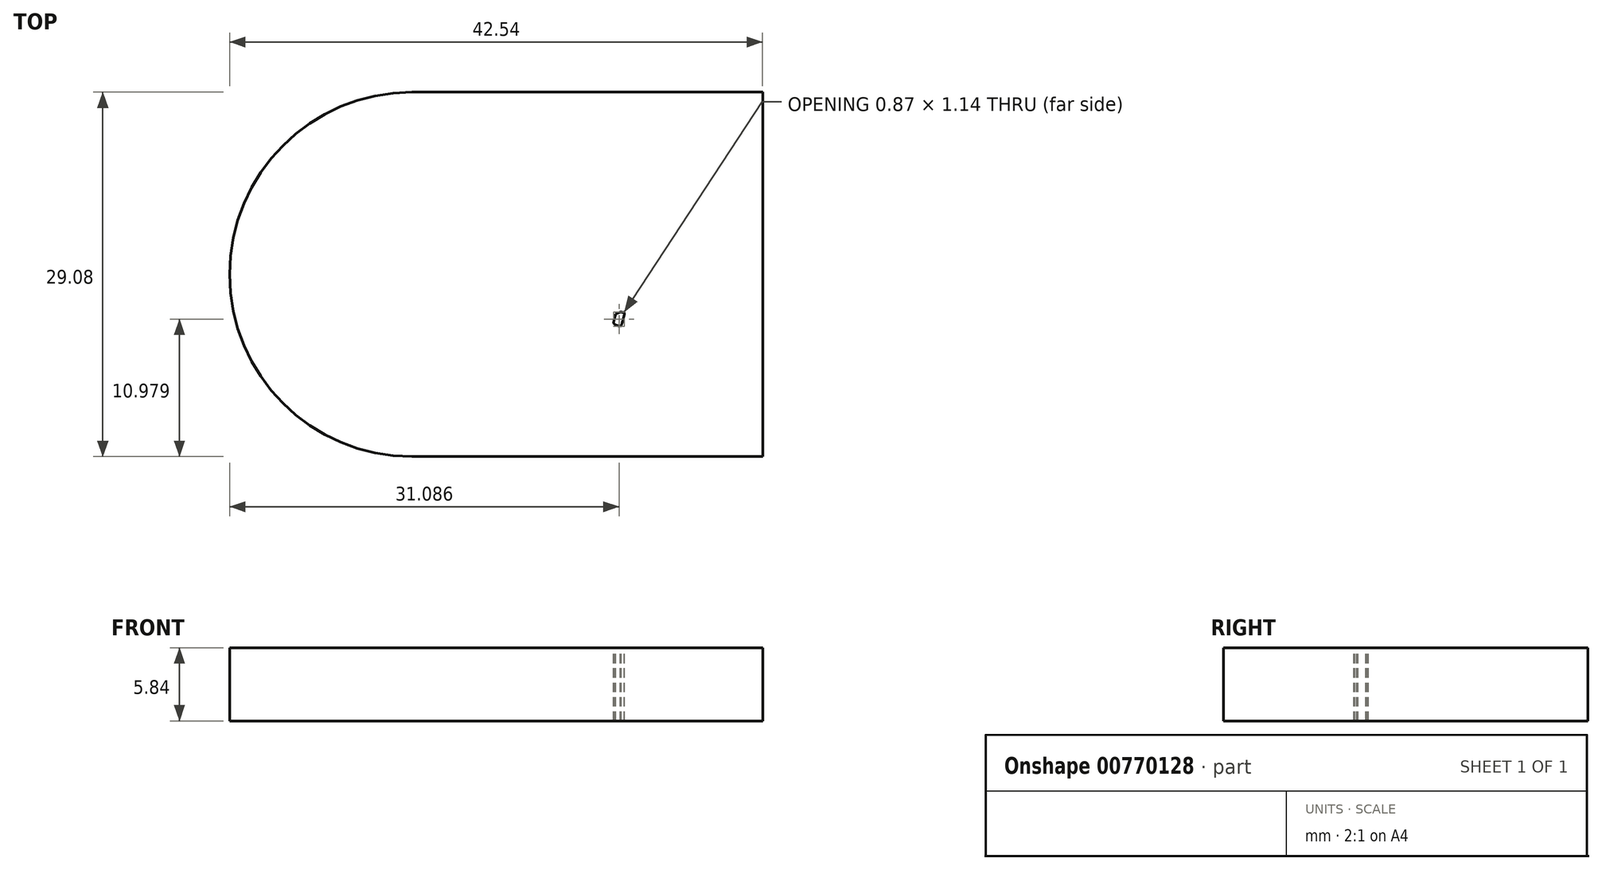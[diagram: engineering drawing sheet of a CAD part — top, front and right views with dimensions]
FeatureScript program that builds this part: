
annotation { "Feature Type Name" : "Feature", "Feature Type Description" : "" }
export const myFeature = defineFeature(function(context is Context, id is Id, definition is map)
    precondition{}
    {
        {
            var Q0;
            Q0=qCreatedBy(makeId("Top.planeOp"),FACE);
            var sketch = newSketch(context, id + "F0", { "sketchPlane" : qUnion([Q0])});
            skLineSegment(sketch, "E0", {"start": v(-14.54, 0) * mm, "end": v(28, 0) * mm, "construction": true});
            skLineSegment(sketch, "E1", {"start": v(0, -14.54) * mm, "end": v(28, -14.54) * mm});
            skLineSegment(sketch, "E2", {"start": v(0, 14.54) * mm, "end": v(28, 14.54) * mm});
            skLineSegment(sketch, "E3", {"start": v(28, -14.54) * mm, "end": v(28, 14.54) * mm});
            skArc(sketch, "E4", {"start": v(0, 14.54) * mm, "mid": v(-14.54, 0) * mm, "end": v(0, -14.54) * mm});
            skSolve(sketch);
        }
        {
            var Q0;
            Q0=makeQuery(id+"F0.imprint","IMPRINT",FACE,{"disambiguationData":[TD([[makeQuery(id+"F0.imprint","IMPRINT",EDGE,{"derivedFrom":sQuery(id+"F0.wireOp",EDGE,"E1")}),1.0]])]});
            extrude(context, id + "F1", {"entities" : qUnion([Q0]), "oppositeDirection" : true, "depth" : 5.84 * mm, "offsetDistance" : 25.4 * mm});
        }
        {
            var Q0;
            Q0=makeQuery(id+"F1.opExtrude","CAP_FACE",FACE,{"disambiguationData":[OSD([sQuery(id+"F0.wireOp",EDGE,"E1"),sQuery(id+"F0.wireOp",EDGE,"E2"),sQuery(id+"F0.wireOp",EDGE,"E3"),sQuery(id+"F0.wireOp",EDGE,"E4")])],"isStart":true});
            var sketch = newSketch(context, id + "F2", { "sketchPlane" : qUnion([Q0])});
            skFitSpline(sketch, "E5", {"points": [v(-3.35, 10.84) * mm, v(-3.23, 11.27) * mm, v(-2.96, 11.36) * mm, v(-2.58, 11.1) * mm]});
            skFitSpline(sketch, "E6", {"points": [v(-2.58, 11.1) * mm, v(-2.42, 11) * mm, v(-2.3, 10.84) * mm, v(-2.1, 10.48) * mm]});
            skFitSpline(sketch, "E7", {"points": [v(-2.1, 10.48) * mm, v(-1.72, 9.81) * mm, v(-1.53, 9.62) * mm, v(-0.8, 9.13) * mm]});
            skFitSpline(sketch, "E8", {"points": [v(-0.8, 9.13) * mm, v(-0.1, 8.66) * mm, v(0.98, 7.86) * mm, v(1.93, 7.1) * mm]});
            skFitSpline(sketch, "E9", {"points": [v(2.93, 6.55) * mm, v(3.7, 6.5) * mm, v(4.42, 6.3) * mm, v(4.64, 6.06) * mm]});
            skFitSpline(sketch, "E10", {"points": [v(4.64, 6.06) * mm, v(4.71, 5.99) * mm, v(5.07, 5.55) * mm, v(5.43, 5.1) * mm]});
            skFitSpline(sketch, "E11", {"points": [v(5.43, 5.1) * mm, v(5.95, 4.45) * mm, v(6.1, 4.23) * mm, v(6.16, 4.02) * mm]});
            skFitSpline(sketch, "E12", {"points": [v(6.16, 4.02) * mm, v(6.2, 3.87) * mm, v(6.34, 3.63) * mm, v(6.48, 3.45) * mm]});
            skFitSpline(sketch, "E13", {"points": [v(6.48, 3.45) * mm, v(6.6, 3.28) * mm, v(6.84, 2.92) * mm, v(7, 2.64) * mm]});
            skFitSpline(sketch, "E14", {"points": [v(7, 2.64) * mm, v(7.2, 2.28) * mm, v(7.3, 2.13) * mm, v(7.42, 2.07) * mm]});
            skFitSpline(sketch, "E15", {"points": [v(7.42, 2.07) * mm, v(7.52, 2.02) * mm, v(7.57, 1.96) * mm, v(7.58, 1.86) * mm]});
            skFitSpline(sketch, "E16", {"points": [v(7.58, 1.86) * mm, v(7.59, 1.75) * mm, v(7.7, 1.6) * mm, v(7.99, 1.31) * mm]});
            skLineSegment(sketch, "E17", {"start": v(1.93, 7.1) * mm, "end": v(2.59, 6.57) * mm});
            skLineSegment(sketch, "E18", {"start": v(2.59, 6.57) * mm, "end": v(2.93, 6.55) * mm});
            skFitSpline(sketch, "E19", {"points": [v(8.64, 0.91) * mm, v(8.87, 0.91) * mm, v(8.92, 0.93) * mm, v(9.07, 1.08) * mm]});
            skFitSpline(sketch, "E20", {"points": [v(9.07, 1.08) * mm, v(9.25, 1.27) * mm, v(9.28, 1.28) * mm, v(9.79, 1.35) * mm]});
            skFitSpline(sketch, "E21", {"points": [v(9.79, 1.35) * mm, v(10.73, 1.49) * mm, v(11, 1.5) * mm, v(12.04, 1.47) * mm]});
            skFitSpline(sketch, "E22", {"points": [v(12.04, 1.47) * mm, v(13.3, 1.44) * mm, v(13.45, 1.46) * mm, v(13.67, 1.72) * mm]});
            skFitSpline(sketch, "E23", {"points": [v(13.67, 1.72) * mm, v(13.84, 1.92) * mm, v(14.3, 2.78) * mm, v(14.68, 3.63) * mm]});
            skFitSpline(sketch, "E24", {"points": [v(14.68, 3.63) * mm, v(14.8, 3.9) * mm, v(14.97, 4.2) * mm, v(15.03, 4.27) * mm]});
            skFitSpline(sketch, "E25", {"points": [v(15.03, 4.27) * mm, v(15.15, 4.4) * mm, v(15.53, 4.55) * mm, v(15.74, 4.55) * mm]});
            skFitSpline(sketch, "E26", {"points": [v(15.74, 4.55) * mm, v(15.8, 4.55) * mm, v(15.92, 4.59) * mm, v(16.02, 4.64) * mm]});
            skFitSpline(sketch, "E27", {"points": [v(16.02, 4.64) * mm, v(16.24, 4.76) * mm, v(16.47, 4.76) * mm, v(16.83, 4.67) * mm]});
            skFitSpline(sketch, "E28", {"points": [v(16.83, 4.67) * mm, v(16.98, 4.63) * mm, v(17.22, 4.6) * mm, v(17.37, 4.6) * mm]});
            skFitSpline(sketch, "E29", {"points": [v(17.37, 4.6) * mm, v(17.82, 4.6) * mm, v(18.4, 4.41) * mm, v(19.13, 4.06) * mm]});
            skFitSpline(sketch, "E30", {"points": [v(19.13, 4.06) * mm, v(19.74, 3.76) * mm, v(20.28, 3.57) * mm, v(20.36, 3.65) * mm]});
            skFitSpline(sketch, "E31", {"points": [v(20.36, 3.65) * mm, v(20.38, 3.67) * mm, v(20.55, 5.16) * mm, v(20.56, 5.4) * mm]});
            skFitSpline(sketch, "E32", {"points": [v(20.56, 5.4) * mm, v(20.56, 5.5) * mm, v(20.94, 5.48) * mm, v(20.98, 5.39) * mm]});
            skFitSpline(sketch, "E33", {"points": [v(20.98, 5.39) * mm, v(21, 5.34) * mm, v(20.97, 4.92) * mm, v(20.93, 4.45) * mm]});
            skLineSegment(sketch, "E34", {"start": v(7.99, 1.31) * mm, "end": v(8.38, 0.91) * mm});
            skLineSegment(sketch, "E35", {"start": v(8.38, 0.91) * mm, "end": v(8.64, 0.91) * mm});
            skFitSpline(sketch, "E36", {"points": [v(21.04, 3.4) * mm, v(21.22, 3.22) * mm, v(21.24, 3.18) * mm, v(21.24, 2.97) * mm]});
            skFitSpline(sketch, "E37", {"points": [v(21.24, 2.97) * mm, v(21.24, 2.84) * mm, v(21.2, 2.6) * mm, v(21.14, 2.45) * mm]});
            skFitSpline(sketch, "E38", {"points": [v(21.14, 2.45) * mm, v(21.05, 2.16) * mm, v(21.05, 2.08) * mm, v(21.16, 2.08) * mm]});
            skFitSpline(sketch, "E39", {"points": [v(21.16, 2.08) * mm, v(21.2, 2.08) * mm, v(21.26, 2.04) * mm, v(21.3, 1.98) * mm]});
            skFitSpline(sketch, "E40", {"points": [v(21.3, 1.98) * mm, v(21.42, 1.86) * mm, v(21.34, 1.82) * mm, v(20.95, 1.79) * mm]});
            skLineSegment(sketch, "E41", {"start": v(20.93, 4.45) * mm, "end": v(20.84, 3.6) * mm});
            skLineSegment(sketch, "E42", {"start": v(20.84, 3.6) * mm, "end": v(21.04, 3.4) * mm});
            skFitSpline(sketch, "E43", {"points": [v(20.6, 1.52) * mm, v(20.58, 1.39) * mm, v(20.43, 0.22) * mm, v(20.27, -1.07) * mm]});
            skFitSpline(sketch, "E44", {"points": [v(20.27, -1.07) * mm, v(19.8, -4.88) * mm, v(19.4, -7.68) * mm, v(19.23, -8.27) * mm]});
            skFitSpline(sketch, "E45", {"points": [v(19.23, -8.27) * mm, v(19.18, -8.45) * mm, v(19.11, -8.56) * mm, v(19, -8.64) * mm]});
            skFitSpline(sketch, "E46", {"points": [v(19, -8.64) * mm, v(18.76, -8.81) * mm, v(18.73, -8.83) * mm, v(18.75, -8.73) * mm]});
            skFitSpline(sketch, "E47", {"points": [v(18.75, -8.73) * mm, v(18.86, -8.26) * mm, v(19.5, -3.67) * mm, v(19.88, -0.54) * mm]});
            skFitSpline(sketch, "E48", {"points": [v(19.88, -0.54) * mm, v(20.02, 0.54) * mm, v(20.14, 1.5) * mm, v(20.15, 1.6) * mm]});
            skFitSpline(sketch, "E49", {"points": [v(20.15, 1.6) * mm, v(20.18, 1.78) * mm, v(20.18, 1.78) * mm, v(20, 1.81) * mm]});
            skFitSpline(sketch, "E50", {"points": [v(20, 1.81) * mm, v(19.72, 1.86) * mm, v(19.5, 1.93) * mm, v(19.5, 1.98) * mm]});
            skFitSpline(sketch, "E51", {"points": [v(19.5, 1.98) * mm, v(19.5, 2.04) * mm, v(19.82, 2.12) * mm, v(20.04, 2.12) * mm]});
            skFitSpline(sketch, "E52", {"points": [v(20.04, 2.12) * mm, v(20.26, 2.12) * mm, v(20.27, 2.18) * mm, v(20.08, 2.4) * mm]});
            skFitSpline(sketch, "E53", {"points": [v(20.08, 2.4) * mm, v(20, 2.49) * mm, v(19.9, 2.65) * mm, v(19.88, 2.75) * mm]});
            skFitSpline(sketch, "E54", {"points": [v(19.88, 2.75) * mm, v(19.81, 2.98) * mm, v(19.82, 2.97) * mm, v(18.94, 3.14) * mm]});
            skFitSpline(sketch, "E55", {"points": [v(18.94, 3.14) * mm, v(18.22, 3.27) * mm, v(17.77, 3.3) * mm, v(17.39, 3.26) * mm]});
            skLineSegment(sketch, "E56", {"start": v(20.95, 1.79) * mm, "end": v(20.63, 1.76) * mm});
            skLineSegment(sketch, "E57", {"start": v(20.63, 1.76) * mm, "end": v(20.6, 1.52) * mm});
            skFitSpline(sketch, "E58", {"points": [v(17.1, 3) * mm, v(17.13, 2.75) * mm, v(17.1, 2.7) * mm, v(16.74, 2.5) * mm]});
            skFitSpline(sketch, "E59", {"points": [v(16.74, 2.5) * mm, v(16.48, 2.36) * mm, v(16.38, 2.08) * mm, v(16.35, 1.4) * mm]});
            skFitSpline(sketch, "E60", {"points": [v(16.35, 1.4) * mm, v(16.32, 0.8) * mm, v(16.32, 0.78) * mm, v(16.17, 0.6) * mm]});
            skFitSpline(sketch, "E61", {"points": [v(16.17, 0.6) * mm, v(16, 0.42) * mm, v(15.95, 0.26) * mm, v(15.86, -0.29) * mm]});
            skFitSpline(sketch, "E62", {"points": [v(15.86, -0.29) * mm, v(15.8, -0.67) * mm, v(15.82, -0.73) * mm, v(16.05, -0.84) * mm]});
            skFitSpline(sketch, "E63", {"points": [v(16.05, -0.84) * mm, v(16.14, -0.88) * mm, v(16.18, -0.95) * mm, v(16.2, -1.05) * mm]});
            skFitSpline(sketch, "E64", {"points": [v(16.2, -1.05) * mm, v(16.22, -1.29) * mm, v(16.38, -1.33) * mm, v(17.24, -1.33) * mm]});
            skFitSpline(sketch, "E65", {"points": [v(17.24, -1.33) * mm, v(18.31, -1.34) * mm, v(18.41, -1.4) * mm, v(18.53, -2.07) * mm]});
            skFitSpline(sketch, "E66", {"points": [v(18.53, -2.07) * mm, v(18.59, -2.42) * mm, v(18.52, -3.18) * mm, v(18.4, -3.43) * mm]});
            skFitSpline(sketch, "E67", {"points": [v(18.4, -3.43) * mm, v(18.3, -3.62) * mm, v(17.83, -3.98) * mm, v(17.47, -4.12) * mm]});
            skFitSpline(sketch, "E68", {"points": [v(17.47, -4.12) * mm, v(17.17, -4.24) * mm, v(16.9, -4.24) * mm, v(16.52, -4.14) * mm]});
            skFitSpline(sketch, "E69", {"points": [v(16.52, -4.14) * mm, v(16.34, -4.1) * mm, v(16.14, -4.08) * mm, v(16, -4.1) * mm]});
            skFitSpline(sketch, "E70", {"points": [v(16, -4.1) * mm, v(15.78, -4.12) * mm, v(15.77, -4.12) * mm, v(15.7, -3.95) * mm]});
            skFitSpline(sketch, "E71", {"points": [v(15.7, -3.95) * mm, v(15.65, -3.86) * mm, v(15.57, -3.77) * mm, v(15.52, -3.75) * mm]});
            skFitSpline(sketch, "E72", {"points": [v(15.52, -3.75) * mm, v(15.37, -3.7) * mm, v(15.1, -3.44) * mm, v(15.1, -3.35) * mm]});
            skFitSpline(sketch, "E73", {"points": [v(15.1, -3.35) * mm, v(15.1, -3.3) * mm, v(15.06, -3.23) * mm, v(15.02, -3.2) * mm]});
            skFitSpline(sketch, "E74", {"points": [v(15.02, -3.2) * mm, v(14.96, -3.16) * mm, v(14.91, -3.18) * mm, v(14.74, -3.34) * mm]});
            skFitSpline(sketch, "E75", {"points": [v(14.74, -3.34) * mm, v(14.56, -3.5) * mm, v(14.51, -3.59) * mm, v(14.46, -3.82) * mm]});
            skFitSpline(sketch, "E76", {"points": [v(14.46, -3.82) * mm, v(14.32, -4.48) * mm, v(14.23, -4.66) * mm, v(13.86, -5.04) * mm]});
            skFitSpline(sketch, "E77", {"points": [v(13.86, -5.04) * mm, v(13.52, -5.39) * mm, v(13.26, -5.75) * mm, v(13.16, -6) * mm]});
            skFitSpline(sketch, "E78", {"points": [v(13.16, -6) * mm, v(13.1, -6.16) * mm, v(12.66, -6.9) * mm, v(12.53, -7.08) * mm]});
            skFitSpline(sketch, "E79", {"points": [v(12.53, -7.08) * mm, v(12.45, -7.17) * mm, v(12.37, -7.22) * mm, v(12.24, -7.23) * mm]});
            skLineSegment(sketch, "E80", {"start": v(17.39, 3.26) * mm, "end": v(17.07, 3.23) * mm});
            skLineSegment(sketch, "E81", {"start": v(17.07, 3.23) * mm, "end": v(17.1, 3) * mm});
            skFitSpline(sketch, "E82", {"points": [v(12.02, -8.1) * mm, v(11.95, -9.47) * mm, v(11.95, -9.58) * mm, v(12.1, -9.83) * mm]});
            skFitSpline(sketch, "E83", {"points": [v(12.1, -9.83) * mm, v(12.22, -10.07) * mm, v(12.35, -10.15) * mm, v(12.76, -10.26) * mm]});
            skFitSpline(sketch, "E84", {"points": [v(12.76, -10.26) * mm, v(12.91, -10.3) * mm, v(13.12, -10.4) * mm, v(13.23, -10.47) * mm]});
            skFitSpline(sketch, "E85", {"points": [v(13.23, -10.47) * mm, v(13.41, -10.62) * mm, v(13.7, -10.97) * mm, v(13.77, -11.12) * mm]});
            skFitSpline(sketch, "E86", {"points": [v(13.77, -11.12) * mm, v(13.81, -11.23) * mm, v(13.56, -11.2) * mm, v(13.44, -11.08) * mm]});
            skLineSegment(sketch, "E87", {"start": v(12.24, -7.23) * mm, "end": v(12.06, -7.24) * mm});
            skLineSegment(sketch, "E88", {"start": v(12.06, -7.24) * mm, "end": v(12.02, -8.1) * mm});
            skFitSpline(sketch, "E89", {"points": [v(13.37, -11.1) * mm, v(13.38, -11.17) * mm, v(13.4, -11.26) * mm, v(13.43, -11.3) * mm]});
            skFitSpline(sketch, "E90", {"points": [v(13.43, -11.3) * mm, v(13.48, -11.46) * mm, v(13.24, -11.38) * mm, v(13.16, -11.23) * mm]});
            skFitSpline(sketch, "E91", {"points": [v(13.16, -11.23) * mm, v(13.13, -11.15) * mm, v(13.07, -11.1) * mm, v(13.03, -11.1) * mm]});
            skFitSpline(sketch, "E92", {"points": [v(13.03, -11.1) * mm, v(12.99, -11.1) * mm, v(12.94, -11.04) * mm, v(12.91, -10.97) * mm]});
            skFitSpline(sketch, "E93", {"points": [v(12.91, -10.97) * mm, v(12.85, -10.81) * mm, v(12.72, -10.75) * mm, v(12.43, -10.75) * mm]});
            skLineSegment(sketch, "E94", {"start": v(13.44, -11.08) * mm, "end": v(13.33, -10.97) * mm});
            skLineSegment(sketch, "E95", {"start": v(13.33, -10.97) * mm, "end": v(13.37, -11.1) * mm});
            skFitSpline(sketch, "E96", {"points": [v(12.35, -10.96) * mm, v(12.55, -11.18) * mm, v(12.55, -11.2) * mm, v(12.46, -11.28) * mm]});
            skFitSpline(sketch, "E97", {"points": [v(12.46, -11.28) * mm, v(12.36, -11.36) * mm, v(12.28, -11.3) * mm, v(12.12, -11.09) * mm]});
            skFitSpline(sketch, "E98", {"points": [v(12.12, -11.09) * mm, v(12.05, -10.98) * mm, v(11.91, -10.86) * mm, v(11.82, -10.82) * mm]});
            skFitSpline(sketch, "E99", {"points": [v(11.82, -10.82) * mm, v(11.58, -10.72) * mm, v(11.47, -10.58) * mm, v(11.43, -10.32) * mm]});
            skFitSpline(sketch, "E100", {"points": [v(11.43, -10.32) * mm, v(11.41, -10.2) * mm, v(11.37, -10.07) * mm, v(11.34, -10.03) * mm]});
            skFitSpline(sketch, "E101", {"points": [v(11.34, -10.03) * mm, v(11.19, -9.85) * mm, v(11.02, -9.42) * mm, v(10.93, -8.96) * mm]});
            skFitSpline(sketch, "E102", {"points": [v(10.93, -8.96) * mm, v(10.84, -8.56) * mm, v(10.82, -8.2) * mm, v(10.8, -7.32) * mm]});
            skFitSpline(sketch, "E103", {"points": [v(10.8, -7.32) * mm, v(10.77, -6.23) * mm, v(10.76, -6.18) * mm, v(10.65, -6.02) * mm]});
            skFitSpline(sketch, "E104", {"points": [v(10.65, -6.02) * mm, v(10.6, -5.93) * mm, v(10.54, -5.83) * mm, v(10.54, -5.8) * mm]});
            skFitSpline(sketch, "E105", {"points": [v(10.54, -5.8) * mm, v(10.54, -5.5) * mm, v(10.86, -5) * mm, v(11.5, -4.3) * mm]});
            skFitSpline(sketch, "E106", {"points": [v(11.5, -4.3) * mm, v(11.62, -4.17) * mm, v(11.7, -4.04) * mm, v(11.69, -4) * mm]});
            skFitSpline(sketch, "E107", {"points": [v(11.69, -4) * mm, v(11.67, -3.97) * mm, v(11.57, -3.92) * mm, v(11.46, -3.9) * mm]});
            skFitSpline(sketch, "E108", {"points": [v(11.46, -3.9) * mm, v(11.3, -3.88) * mm, v(11.22, -3.82) * mm, v(11.03, -3.59) * mm]});
            skFitSpline(sketch, "E109", {"points": [v(11.03, -3.59) * mm, v(10.7, -3.22) * mm, v(10.57, -3.16) * mm, v(10.2, -3.27) * mm]});
            skFitSpline(sketch, "E110", {"points": [v(10.2, -3.27) * mm, v(9.84, -3.37) * mm, v(9.8, -3.37) * mm, v(9.63, -3.2) * mm]});
            skFitSpline(sketch, "E111", {"points": [v(9.63, -3.2) * mm, v(9.45, -3.05) * mm, v(9.27, -3) * mm, v(9, -3.04) * mm]});
            skFitSpline(sketch, "E112", {"points": [v(9, -3.04) * mm, v(8.89, -3.05) * mm, v(8.73, -3.07) * mm, v(8.64, -3.07) * mm]});
            skFitSpline(sketch, "E113", {"points": [v(8.64, -3.07) * mm, v(8.51, -3.08) * mm, v(8.47, -3.12) * mm, v(8.34, -3.33) * mm]});
            skFitSpline(sketch, "E114", {"points": [v(8.34, -3.33) * mm, v(8.26, -3.47) * mm, v(8.14, -3.64) * mm, v(8.08, -3.71) * mm]});
            skFitSpline(sketch, "E115", {"points": [v(8.08, -3.71) * mm, v(7.93, -3.88) * mm, v(7.66, -4.47) * mm, v(7.41, -5.14) * mm]});
            skFitSpline(sketch, "E116", {"points": [v(7.41, -5.14) * mm, v(7.2, -5.72) * mm, v(6.8, -6.51) * mm, v(6.5, -6.98) * mm]});
            skFitSpline(sketch, "E117", {"points": [v(6.5, -6.98) * mm, v(6.31, -7.25) * mm, v(6.18, -7.38) * mm, v(5.76, -7.68) * mm]});
            skFitSpline(sketch, "E118", {"points": [v(5.76, -7.68) * mm, v(5, -8.23) * mm, v(4.87, -8.29) * mm, v(4.48, -8.34) * mm]});
            skFitSpline(sketch, "E119", {"points": [v(4.48, -8.34) * mm, v(4.28, -8.36) * mm, v(3.82, -8.47) * mm, v(3.45, -8.57) * mm]});
            skFitSpline(sketch, "E120", {"points": [v(3.45, -8.57) * mm, v(3.07, -8.68) * mm, v(2.72, -8.77) * mm, v(2.67, -8.77) * mm]});
            skFitSpline(sketch, "E121", {"points": [v(2.67, -8.77) * mm, v(2.55, -8.77) * mm, v(2, -8.33) * mm, v(1.82, -8.08) * mm]});
            skFitSpline(sketch, "E122", {"points": [v(1.82, -8.08) * mm, v(1.75, -8) * mm, v(1.66, -7.84) * mm, v(1.62, -7.75) * mm]});
            skFitSpline(sketch, "E123", {"points": [v(1.62, -7.75) * mm, v(1.55, -7.59) * mm, v(1.53, -7.58) * mm, v(0.88, -7.4) * mm]});
            skFitSpline(sketch, "E124", {"points": [v(0.88, -7.4) * mm, v(0, -7.14) * mm, v(-0.84, -6.98) * mm, v(-1.22, -6.98) * mm]});
            skFitSpline(sketch, "E125", {"points": [v(-1.22, -6.98) * mm, v(-1.47, -6.98) * mm, v(-1.54, -7) * mm, v(-1.64, -7.1) * mm]});
            skFitSpline(sketch, "E126", {"points": [v(-1.64, -7.1) * mm, v(-1.82, -7.28) * mm, v(-2.33, -8.36) * mm, v(-2.4, -8.74) * mm]});
            skFitSpline(sketch, "E127", {"points": [v(-2.4, -8.74) * mm, v(-2.44, -8.92) * mm, v(-2.5, -9.09) * mm, v(-2.54, -9.11) * mm]});
            skFitSpline(sketch, "E128", {"points": [v(-2.54, -9.11) * mm, v(-2.64, -9.18) * mm, v(-2.84, -9.1) * mm, v(-2.98, -8.96) * mm]});
            skFitSpline(sketch, "E129", {"points": [v(-2.98, -8.96) * mm, v(-3.14, -8.8) * mm, v(-3.14, -8.77) * mm, v(-3.04, -8.26) * mm]});
            skFitSpline(sketch, "E130", {"points": [v(-3.04, -8.26) * mm, v(-2.92, -7.62) * mm, v(-2.77, -6.42) * mm, v(-2.77, -6.02) * mm]});
            skLineSegment(sketch, "E131", {"start": v(12.43, -10.75) * mm, "end": v(12.18, -10.75) * mm});
            skLineSegment(sketch, "E132", {"start": v(12.18, -10.75) * mm, "end": v(12.35, -10.96) * mm});
            skFitSpline(sketch, "E133", {"points": [v(-2.56, -5.44) * mm, v(-2.36, -5.24) * mm, v(-2.33, -5.23) * mm, v(-2.13, -5.25) * mm]});
            skFitSpline(sketch, "E134", {"points": [v(-2.13, -5.25) * mm, v(-2.02, -5.26) * mm, v(-1.67, -5.37) * mm, v(-1.35, -5.48) * mm]});
            skLineSegment(sketch, "E135", {"start": v(-2.77, -6.02) * mm, "end": v(-2.77, -5.66) * mm});
            skLineSegment(sketch, "E136", {"start": v(-2.77, -5.66) * mm, "end": v(-2.56, -5.44) * mm});
            skFitSpline(sketch, "E137", {"points": [v(0.2, -5.73) * mm, v(0.74, -5.75) * mm, v(1.38, -5.79) * mm, v(1.63, -5.81) * mm]});
            skFitSpline(sketch, "E138", {"points": [v(1.63, -5.81) * mm, v(2.04, -5.86) * mm, v(2.1, -5.85) * mm, v(2.14, -5.78) * mm]});
            skFitSpline(sketch, "E139", {"points": [v(2.14, -5.78) * mm, v(2.16, -5.73) * mm, v(2.24, -5.63) * mm, v(2.32, -5.56) * mm]});
            skFitSpline(sketch, "E140", {"points": [v(2.32, -5.56) * mm, v(2.45, -5.42) * mm, v(2.47, -5.42) * mm, v(2.81, -5.45) * mm]});
            skFitSpline(sketch, "E141", {"points": [v(2.81, -5.45) * mm, v(3.16, -5.48) * mm, v(3.17, -5.48) * mm, v(3.28, -5.35) * mm]});
            skFitSpline(sketch, "E142", {"points": [v(3.28, -5.35) * mm, v(3.5, -5.06) * mm, v(4.28, -3.4) * mm, v(4.53, -2.66) * mm]});
            skLineSegment(sketch, "E143", {"start": v(-1.35, -5.48) * mm, "end": v(-0.77, -5.69) * mm});
            skLineSegment(sketch, "E144", {"start": v(-0.77, -5.69) * mm, "end": v(0.2, -5.73) * mm});
            skFitSpline(sketch, "E145", {"points": [v(4.64, -1.52) * mm, v(4.48, -1.11) * mm, v(3.8, 0.14) * mm, v(3.48, 0.62) * mm]});
            skFitSpline(sketch, "E146", {"points": [v(3.48, 0.62) * mm, v(3.37, 0.77) * mm, v(3.2, 0.97) * mm, v(3.11, 1.04) * mm]});
            skFitSpline(sketch, "E147", {"points": [v(3.11, 1.04) * mm, v(2.91, 1.21) * mm, v(2.7, 1.53) * mm, v(2.7, 1.65) * mm]});
            skFitSpline(sketch, "E148", {"points": [v(2.7, 1.65) * mm, v(2.7, 1.81) * mm, v(2.43, 2.26) * mm, v(1.99, 2.85) * mm]});
            skFitSpline(sketch, "E149", {"points": [v(1.99, 2.85) * mm, v(1.36, 3.69) * mm, v(1.21, 4.07) * mm, v(1.36, 4.49) * mm]});
            skLineSegment(sketch, "E150", {"start": v(4.53, -2.66) * mm, "end": v(4.78, -1.9) * mm});
            skLineSegment(sketch, "E151", {"start": v(4.78, -1.9) * mm, "end": v(4.64, -1.52) * mm});
            skFitSpline(sketch, "E152", {"points": [v(1.05, 4.96) * mm, v(0.45, 5.38) * mm, v(-0.05, 5.96) * mm, v(-1.03, 7.4) * mm]});
            skFitSpline(sketch, "E153", {"points": [v(-1.03, 7.4) * mm, v(-1.87, 8.62) * mm, v(-1.86, 8.62) * mm, v(-2.38, 8.81) * mm]});
            skFitSpline(sketch, "E154", {"points": [v(-2.38, 8.81) * mm, v(-2.47, 8.85) * mm, v(-2.68, 8.96) * mm, v(-2.83, 9.06) * mm]});
            skFitSpline(sketch, "E155", {"points": [v(-2.83, 9.06) * mm, v(-3.23, 9.32) * mm, v(-3.37, 9.63) * mm, v(-3.39, 10.23) * mm]});
            skFitSpline(sketch, "E156", {"points": [v(-3.39, 10.23) * mm, v(-3.4, 10.47) * mm, v(-3.38, 10.75) * mm, v(-3.35, 10.84) * mm]});
            skLineSegment(sketch, "E157", {"start": v(1.36, 4.49) * mm, "end": v(1.43, 4.7) * mm});
            skLineSegment(sketch, "E158", {"start": v(1.43, 4.7) * mm, "end": v(1.05, 4.96) * mm});
            skFitSpline(sketch, "E159", {"points": [v(16.15, -3.92) * mm, v(16.2, -3.99) * mm, v(16.68, -4.13) * mm, v(16.7, -4.08) * mm]});
            skFitSpline(sketch, "E160", {"points": [v(16.7, -4.08) * mm, v(16.74, -4.02) * mm, v(16.98, -3.09) * mm, v(16.96, -3.07) * mm]});
            skFitSpline(sketch, "E161", {"points": [v(16.96, -3.07) * mm, v(16.96, -3.07) * mm, v(16.82, -3.03) * mm, v(16.65, -2.99) * mm]});
            skFitSpline(sketch, "E162", {"points": [v(16.28, -3.17) * mm, v(16.22, -3.39) * mm, v(16.13, -3.74) * mm, v(16.11, -3.83) * mm]});
            skFitSpline(sketch, "E163", {"points": [v(16.11, -3.83) * mm, v(16.11, -3.84) * mm, v(16.13, -3.88) * mm, v(16.15, -3.92) * mm]});
            skLineSegment(sketch, "E164", {"start": v(16.28, -3.17) * mm, "end": v(16.65, -2.99) * mm});
            skSolve(sketch);
        }
        {
            var Q0;
            Q0 = qSketchRegion(id + "F2", true);
            extrude(context, id + "F3", {"entities" : qUnion([Q0]), "operationType" : NewBodyOperationType.REMOVE, "oppositeDirection" : true, "depth" : 25.4 * mm, "offsetDistance" : 25.4 * mm});
        }
    });
